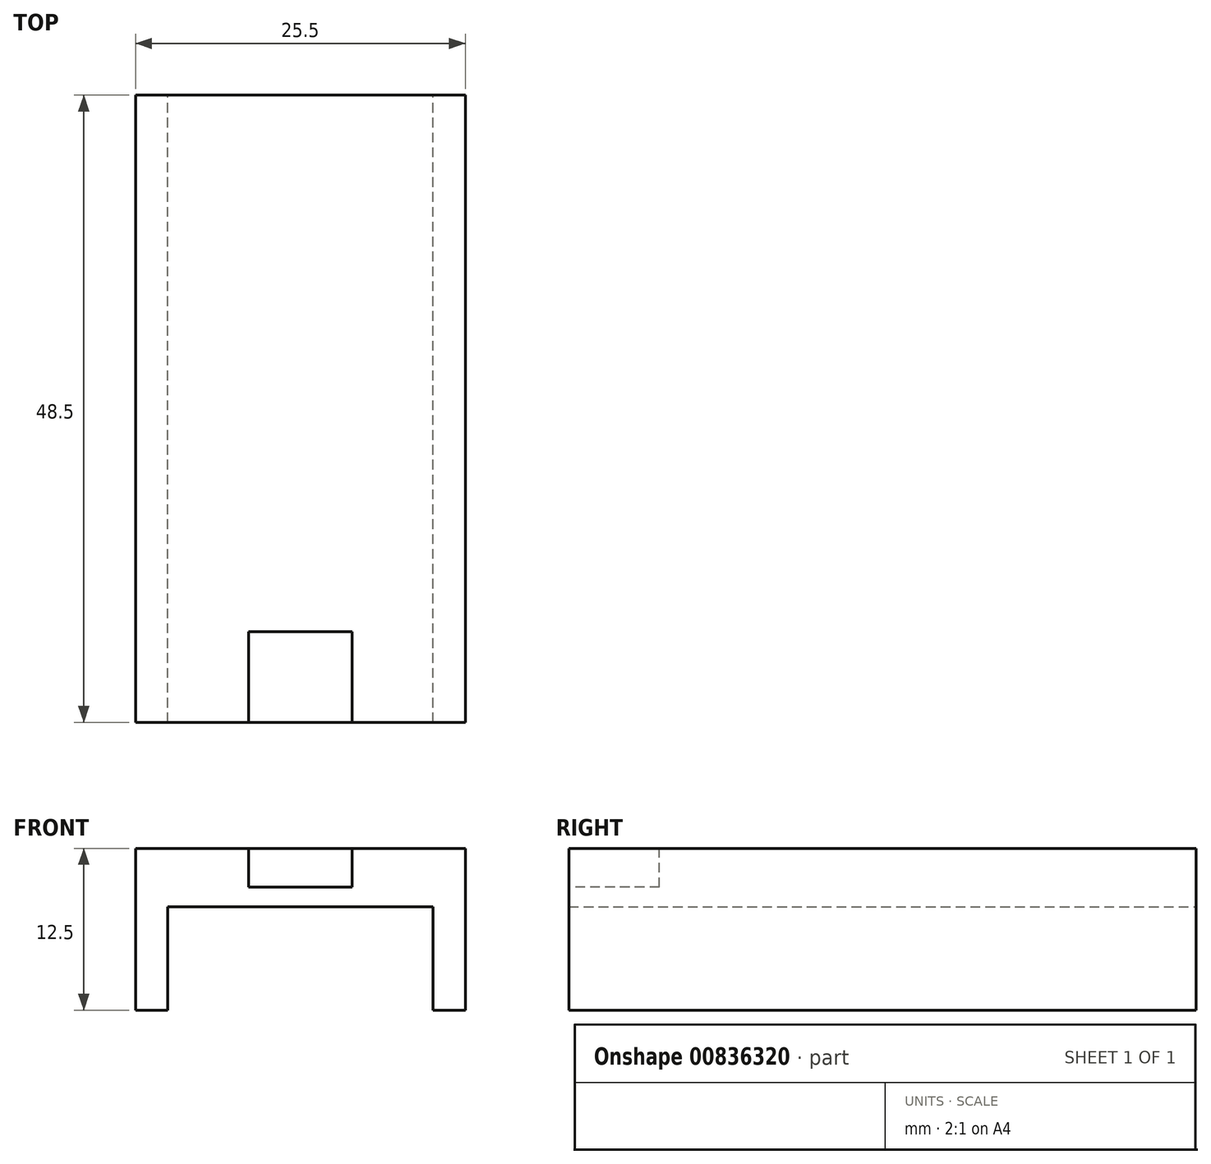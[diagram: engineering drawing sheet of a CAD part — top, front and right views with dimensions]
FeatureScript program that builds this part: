
annotation { "Feature Type Name" : "Feature", "Feature Type Description" : "" }
export const myFeature = defineFeature(function(context is Context, id is Id, definition is map)
    precondition{}
    {
        {
            var Q0;
            Q0=qCreatedBy(makeId("Front.planeOp"),FACE);
            var sketch = newSketch(context, id + "F0", { "sketchPlane" : qUnion([Q0])});
            skLineSegment(sketch, "E0.bottom", {"start": v(-12.75, 8) * mm, "end": v(12.75, 8) * mm});
            skLineSegment(sketch, "E0.top", {"start": v(-12.75, 12.5) * mm, "end": v(12.75, 12.5) * mm});
            skLineSegment(sketch, "E0.left", {"start": v(-12.75, 8) * mm, "end": v(-12.75, 12.5) * mm});
            skLineSegment(sketch, "E0.right", {"start": v(12.75, 8) * mm, "end": v(12.75, 12.5) * mm});
            skPoint(sketch, "E1", {"position": v(0, 12.5) * mm});
            skLineSegment(sketch, "E2.bottom", {"start": v(12.75, 8) * mm, "end": v(10.25, 8) * mm});
            skLineSegment(sketch, "E2.top", {"start": v(12.75, 0) * mm, "end": v(10.25, 0) * mm});
            skLineSegment(sketch, "E2.left", {"start": v(12.75, 8) * mm, "end": v(12.75, 0) * mm});
            skLineSegment(sketch, "E2.right", {"start": v(10.25, 8) * mm, "end": v(10.25, 0) * mm});
            skLineSegment(sketch, "E3.bottom", {"start": v(-12.75, 8) * mm, "end": v(-10.25, 8) * mm});
            skLineSegment(sketch, "E3.top", {"start": v(-12.75, 0) * mm, "end": v(-10.25, 0) * mm});
            skLineSegment(sketch, "E3.left", {"start": v(-12.75, 8) * mm, "end": v(-12.75, 0) * mm});
            skLineSegment(sketch, "E3.right", {"start": v(-10.25, 8) * mm, "end": v(-10.25, 0) * mm});
            skSolve(sketch);
        }
        {
            var Q0;
            Q0=qSketchRegion(id+"F0",true);
            extrude(context, id + "F1", {"entities" : qUnion([Q0]), "endBound" : BoundingType.SYMMETRIC, "depth" : 48.5 * mm, "offsetDistance" : 25 * mm});
        }
        {
            var Q0;
            Q0=makeQuery(id+"F1.opExtrude","CAP_FACE",FACE,{"disambiguationData":[OSD([sQuery(id+"F0.wireOp",EDGE,"E0.bottom"),sQuery(id+"F0.wireOp",EDGE,"E0.top"),sQuery(id+"F0.wireOp",EDGE,"E0.left"),sQuery(id+"F0.wireOp",EDGE,"E0.right"),sQuery(id+"F0.wireOp",EDGE,"E2.top"),sQuery(id+"F0.wireOp",EDGE,"E2.left"),sQuery(id+"F0.wireOp",EDGE,"E2.right"),sQuery(id+"F0.wireOp",EDGE,"E3.top"),sQuery(id+"F0.wireOp",EDGE,"E3.left"),sQuery(id+"F0.wireOp",EDGE,"E3.right")])],"isStart":false});
            var sketch = newSketch(context, id + "F2", { "sketchPlane" : qUnion([Q0])});
            skLineSegment(sketch, "E4.bottom", {"start": v(-4, 9.5) * mm, "end": v(4, 9.5) * mm});
            skLineSegment(sketch, "E4.top", {"start": v(-4, 12.5) * mm, "end": v(4, 12.5) * mm});
            skLineSegment(sketch, "E4.left", {"start": v(-4, 9.5) * mm, "end": v(-4, 12.5) * mm});
            skLineSegment(sketch, "E4.right", {"start": v(4, 9.5) * mm, "end": v(4, 12.5) * mm});
            skPoint(sketch, "E5", {"position": v(0, 9.5) * mm});
            skSolve(sketch);
        }
        {
            var Q0;
            Q0=qSketchRegion(id+"F2",true);
            extrude(context, id + "F3", {"entities" : qUnion([Q0]), "operationType" : NewBodyOperationType.REMOVE, "oppositeDirection" : true, "depth" : 7 * mm, "offsetDistance" : 25 * mm});
        }
    });
